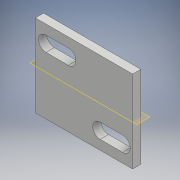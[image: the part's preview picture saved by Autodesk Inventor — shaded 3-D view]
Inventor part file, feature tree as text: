
AUTODESK INVENTOR PART (.ipt)
format: ipt  version: 2017 (Build 210142000, 142)  size: 114,176 bytes
history: native  units: mm
features: extrude x1, plane x1, sketch x1
ambient origin geometry x8: Origin, YZ Plane, XZ Plane, XY Plane, X Axis, Y Axis, Z Axis, Center Point
bodies: Solid1 (feature_tree)
feature tree (3):
  extrude  "Extrusion1"  Depth=22.0mm
  plane  "Work Plane1"
  sketch  "Sketch1"  dims[d0=26.0mm d1=22.0mm d5=6.0mm d6=4.0mm d9=2.2mm d10=0.0mm d16=6.0mm d17=4.0mm d18=14.5mm]
